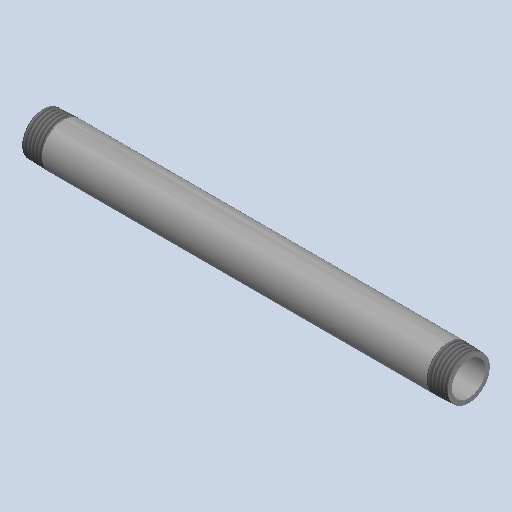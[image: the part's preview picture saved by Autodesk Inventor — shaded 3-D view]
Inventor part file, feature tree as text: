
AUTODESK INVENTOR PART (.ipt)
format: ipt  version: 2025 (Build 290162000, 162)  size: 169,984 bytes
history: native  units: mm (DEFAULTED — no unit token found)
features: other x8, revolve x1
ambient origin geometry x8: Origin, YZ Plane, XZ Plane, XY Plane, X Axis, Y Axis, Z Axis, Center Point
bodies: Solid1 (feature_tree)
feature tree (9):
  revolve  "Revolution1"  [1 undecoded]
  other  "Work Axis1"
  other  "Work Point5"
  other  "Work Axis2"
  other  "Work Point6"
  other  "Work Axis3"
  other  "Work Axis4"
  other  "Work Point7"
  other  "Work Point8"
note: 1 required parameter value undecoded (feature->parameter linkage not recoverable at this tier; creation-order binding heuristic only, values carry confidence <= 0.55)
